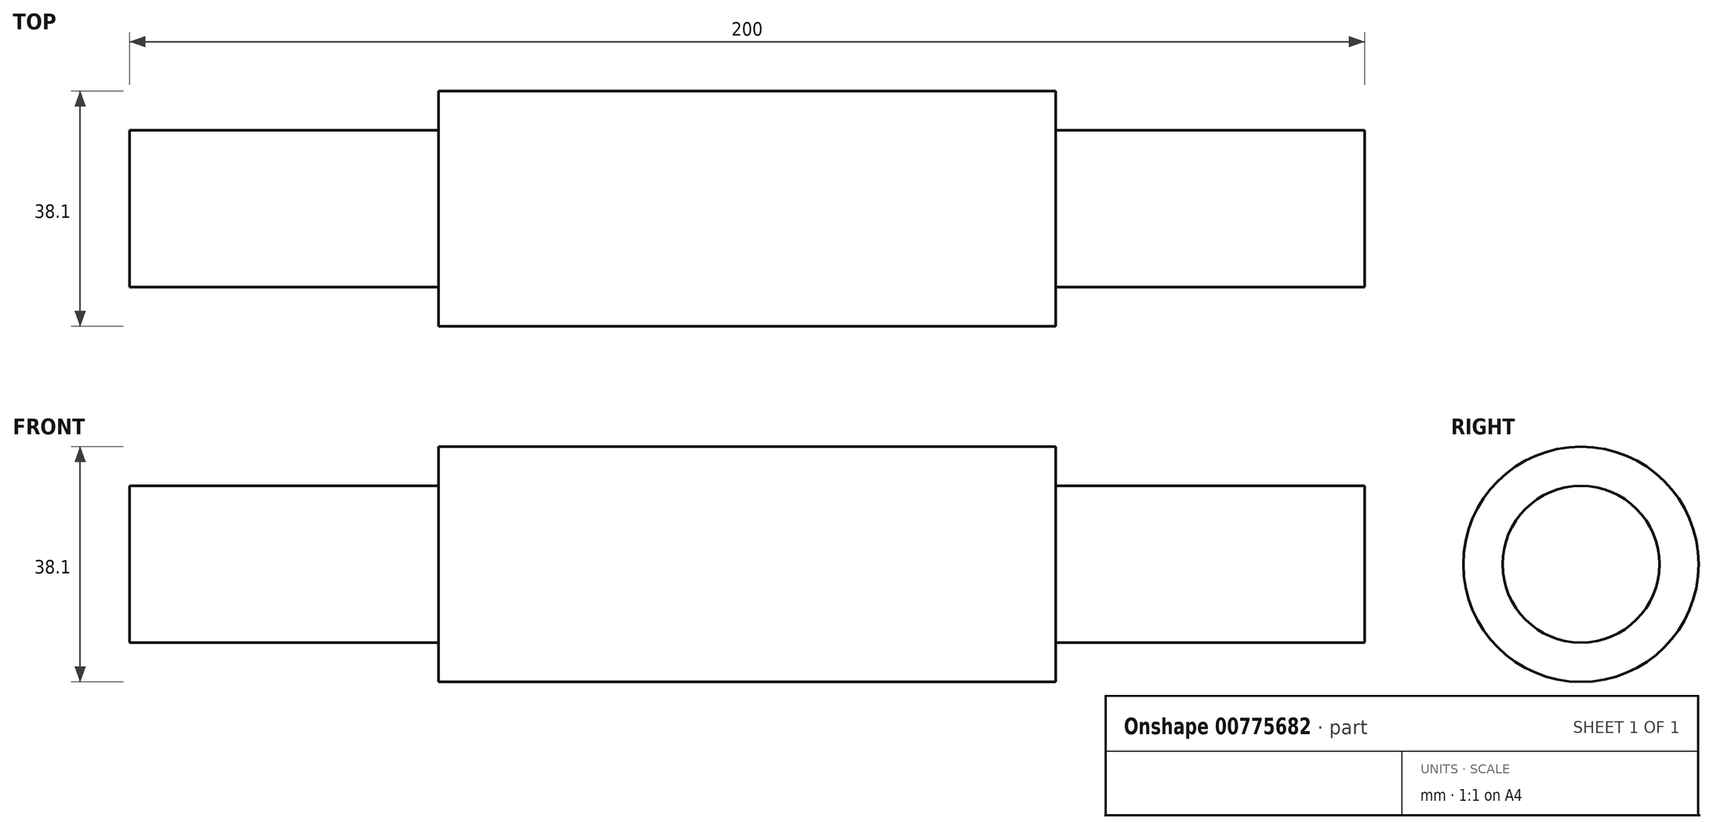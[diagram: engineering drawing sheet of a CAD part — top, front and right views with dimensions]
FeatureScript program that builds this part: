
annotation { "Feature Type Name" : "Feature", "Feature Type Description" : "" }
export const myFeature = defineFeature(function(context is Context, id is Id, definition is map)
    precondition{}
    {
        {
            var Q0;
            Q0=qCreatedBy(makeId("Front.planeOp"),FACE);
            var sketch = newSketch(context, id + "F0", { "sketchPlane" : qUnion([Q0])});
            skLineSegment(sketch, "E0", {"start": v(-95.96, 0) * mm, "end": v(104.04, 0) * mm});
            skLineSegment(sketch, "E1", {"start": v(104.04, 0) * mm, "end": v(104.04, 12.7) * mm});
            skLineSegment(sketch, "E2", {"start": v(104.04, 12.7) * mm, "end": v(54.04, 12.7) * mm});
            skLineSegment(sketch, "E3", {"start": v(54.04, 12.7) * mm, "end": v(54.04, 19.05) * mm});
            skLineSegment(sketch, "E4", {"start": v(54.04, 19.05) * mm, "end": v(-45.96, 19.05) * mm});
            skLineSegment(sketch, "E5", {"start": v(-45.96, 19.05) * mm, "end": v(-45.96, 12.7) * mm});
            skLineSegment(sketch, "E6", {"start": v(-45.96, 12.7) * mm, "end": v(-95.96, 12.7) * mm});
            skLineSegment(sketch, "E7", {"start": v(-95.96, 12.7) * mm, "end": v(-95.96, 0) * mm});
            skSolve(sketch);
        }
        {
            var Q0;
            Q0=makeQuery(id+"F0.imprint","IMPRINT",FACE,{"disambiguationData":[TD([[makeQuery(id+"F0.imprint","IMPRINT",EDGE,{"derivedFrom":sQuery(id+"F0.wireOp",EDGE,"E0")}),1.0]])]});
            var Q1;
            Q1=sQuery(id+"F0.wireOp",EDGE,"E0");
            revolve(context, id + "F1", {"surfaceOperationType" : NewSurfaceOperationType.NEW, "entities" : qUnion([Q0]), "axis" : qUnion([Q1]), "revolveType" : RevolveType.FULL});
        }
    });
